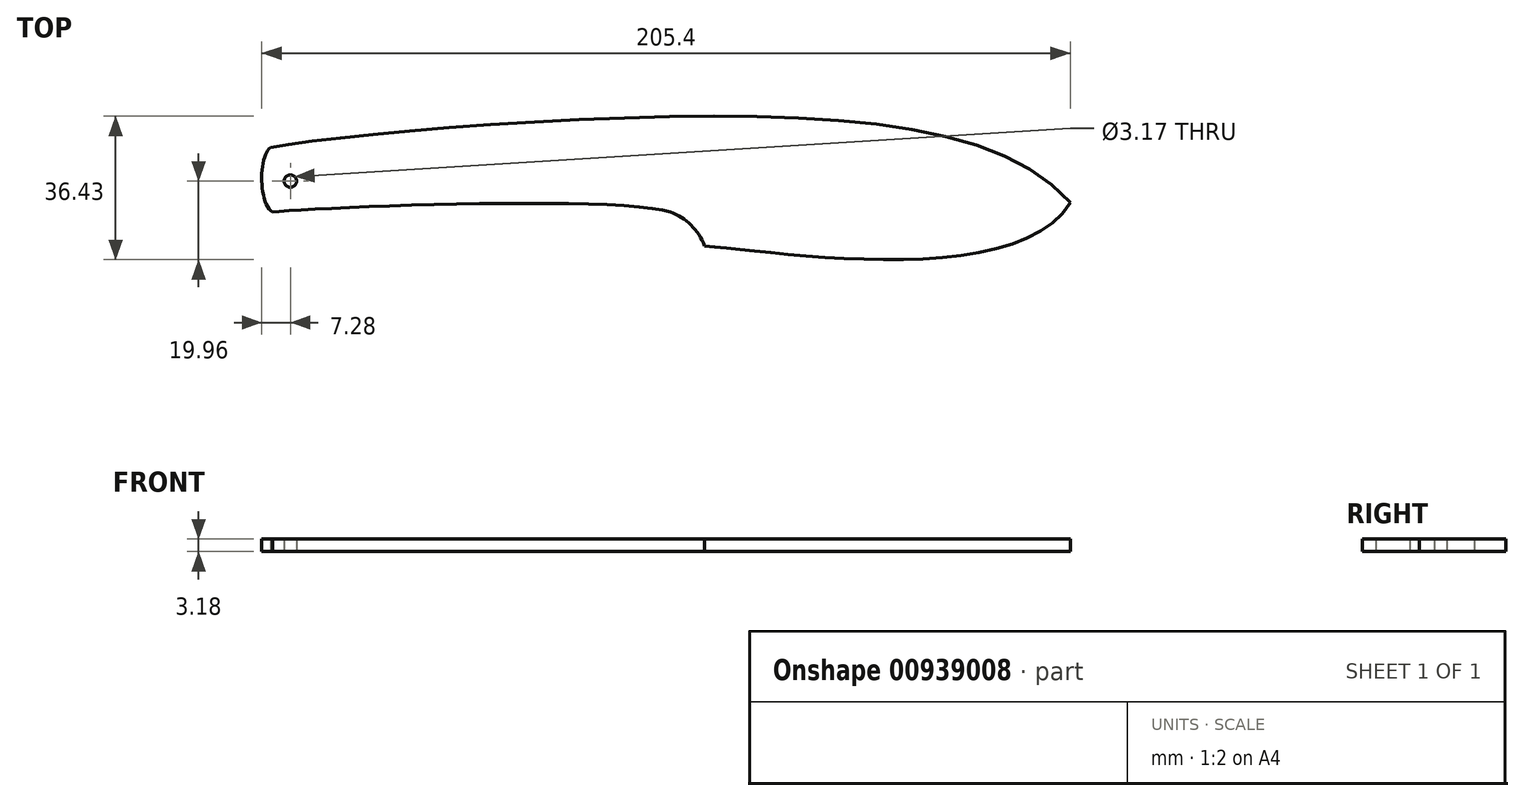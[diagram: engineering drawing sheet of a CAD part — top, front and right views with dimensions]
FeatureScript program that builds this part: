
annotation { "Feature Type Name" : "Feature", "Feature Type Description" : "" }
export const myFeature = defineFeature(function(context is Context, id is Id, definition is map)
    precondition{}
    {
        {
            var Q0;
            Q0=qCreatedBy(makeId("Top.planeOp"),FACE);
            var sketch = newSketch(context, id + "F0", { "sketchPlane" : qUnion([Q0])});
            skCircle(sketch, "E0", {"center": v(0, 0) * mm, "radius": 1.59 * mm});
            skFitSpline(sketch, "E1", {"points": [v(198.12, -5.43) * mm, v(109.2, 16.47) * mm, v(-5.08, 8.53) * mm], "startDerivative": vector(-99.23, 113.12) * mm, "endDerivative": vector(-88.58, -16.7) * mm});
            skFitSpline(sketch, "E2", {"points": [v(198.12, -5.43) * mm, v(105.21, -16.45) * mm], "startDerivative": vector(-40.66, -67.77) * mm, "endDerivative": vector(-53.15, 4.33) * mm});
            skFitSpline(sketch, "E3", {"points": [v(-5.08, 8.53) * mm, v(-4.5, -7.89) * mm], "startDerivative": vector(-8.59, -5.89) * mm, "endDerivative": vector(11.28, -7.36) * mm});
            skFitSpline(sketch, "E4", {"points": [v(-4.5, -7.89) * mm, v(96.52, -7.89) * mm], "startDerivative": vector(30.65, 3.56) * mm, "endDerivative": vector(37.1, -13.19) * mm});
            skArc(sketch, "E5", {"start": v(105.21, -16.45) * mm, "mid": v(101.82, -11.2) * mm, "end": v(96.52, -7.89) * mm});
            skSolve(sketch);
        }
        {
            var Q0;
            Q0=makeQuery(id+"F0.imprint","IMPRINT",FACE,{"disambiguationData":[TD([[makeQuery(id+"F0.imprint","IMPRINT",EDGE,{"derivedFrom":sQuery(id+"F0.wireOp",EDGE,"E0")}),-1.0]])]});
            extrude(context, id + "F1", {"entities" : qUnion([Q0]), "depth" : 3.17 * mm, "offsetDistance" : 25.4 * mm});
        }
    });
